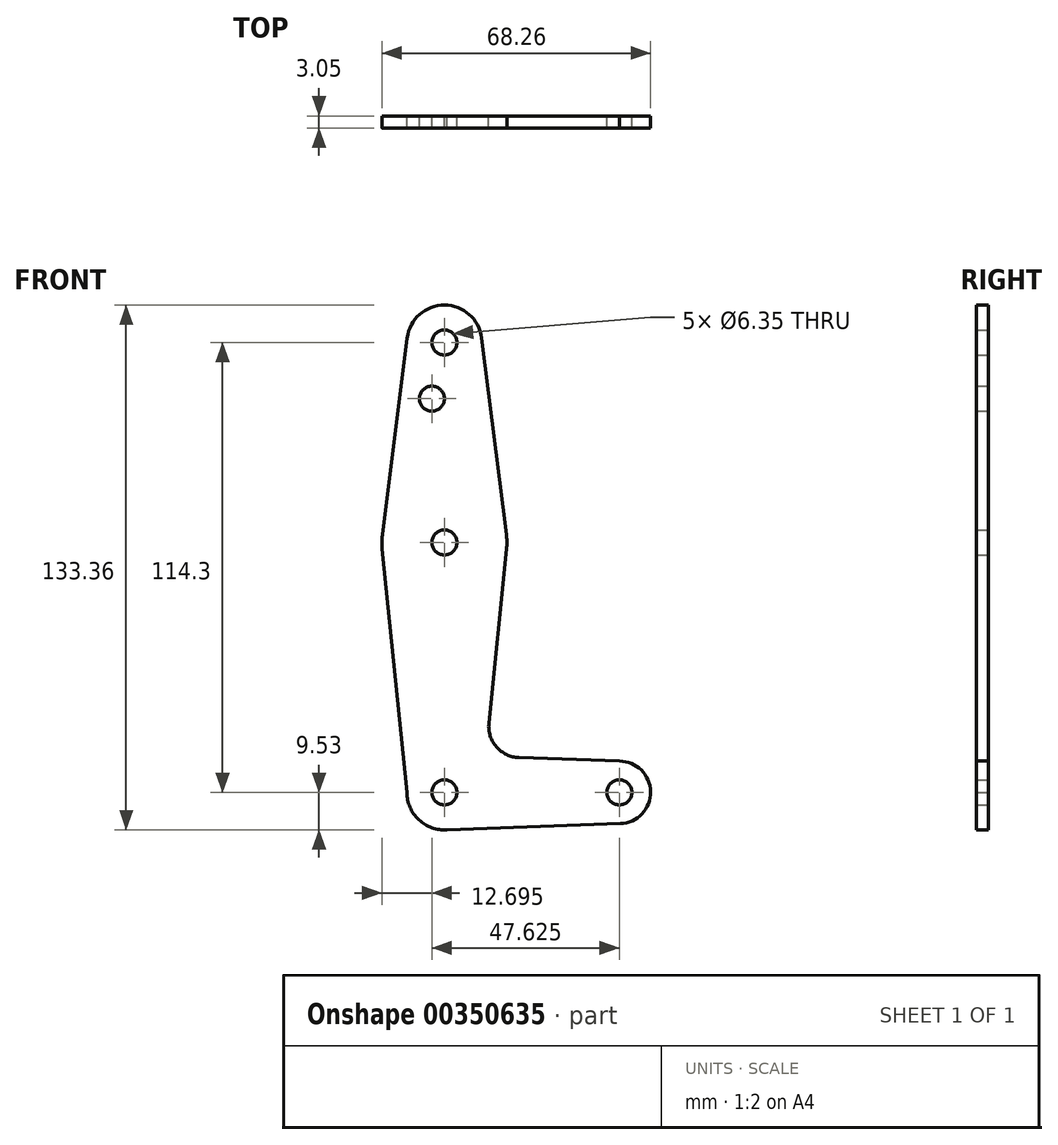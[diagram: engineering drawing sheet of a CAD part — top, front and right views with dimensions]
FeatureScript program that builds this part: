
annotation { "Feature Type Name" : "Feature", "Feature Type Description" : "" }
export const myFeature = defineFeature(function(context is Context, id is Id, definition is map)
    precondition{}
    {
        {
            var Q0;
            Q0=qCreatedBy(makeId("Front.planeOp"),FACE);
            var sketch = newSketch(context, id + "F0", { "sketchPlane" : qUnion([Q0])});
            skLineSegment(sketch, "E0", {"start": v(0, 0) * mm, "end": v(0, 114.3) * mm, "construction": true});
            skLineSegment(sketch, "E1", {"start": v(0, 0) * mm, "end": v(44.45, 0) * mm, "construction": true});
            skCircle(sketch, "E2", {"center": v(0, 114.3) * mm, "radius": 9.53 * mm});
            skCircle(sketch, "E3", {"center": v(0, 63.5) * mm, "radius": 15.88 * mm});
            skCircle(sketch, "E4", {"center": v(0, 0) * mm, "radius": 9.53 * mm});
            skCircle(sketch, "E5", {"center": v(44.45, 0) * mm, "radius": 7.94 * mm});
            skLineSegment(sketch, "E6", {"start": v(-15.75, 65.48) * mm, "end": v(-9.45, 115.5) * mm});
            skLineSegment(sketch, "E7", {"start": v(-9.53, 0) * mm, "end": v(-15.8, 61.9) * mm});
            skLineSegment(sketch, "E8", {"start": v(9.45, 115.5) * mm, "end": v(16, 63.5) * mm});
            skLineSegment(sketch, "E9", {"start": v(15.8, 61.9) * mm, "end": v(11.3, 17.6) * mm});
            skLineSegment(sketch, "E10", {"start": v(18.93, 8.85) * mm, "end": v(44.45, 7.94) * mm});
            skLineSegment(sketch, "E11", {"start": v(0, -9.53) * mm, "end": v(44.73, -7.93) * mm});
            skCircle(sketch, "E12", {"center": v(0, 114.3) * mm, "radius": 3.18 * mm});
            skCircle(sketch, "E13", {"center": v(0, 63.5) * mm, "radius": 3.18 * mm});
            skCircle(sketch, "E14", {"center": v(0, 0) * mm, "radius": 3.18 * mm});
            skCircle(sketch, "E15", {"center": v(44.45, 0) * mm, "radius": 3.18 * mm});
            skCircle(sketch, "E16", {"center": v(-3.18, 100.03) * mm, "radius": 3.18 * mm});
            skArc(sketch, "E17.filletArc", {"start": v(11.3, 17.6) * mm, "mid": v(13.22, 11.57) * mm, "end": v(18.93, 8.85) * mm});
            skSolve(sketch);
        }
        {
            var Q0;
            Q0 = qSketchRegion(id + "F0", true);
            extrude(context, id + "F1", {"entities" : qUnion([Q0]), "depth" : 3.05 * mm});
        }
    });
